FCSTD DOCUMENT  (FreeCAD 0.21RUnknown)
Label: m12_battery_holder
License: All rights reserved
LicenseURL: http://en.wikipedia.org/wiki/All_rights_reserved
objects: Sketcher::SketchObject×1, PartDesign::Body×1, Spreadsheet::Sheet×1
note: 2 computed .brp shape members not serialized (recipe doc carries the construction recipe); baked Part::Feature solids carry a one-line shape summary decoded from their .brp

FEATURE [Sketcher::SketchObject] Sketch002
  FullyConstrained = true
  MapMode = 5
  Support = -> [XY_Plane]
  expr: Constraints[22] = Spreadsheet.Diameter
  expr: Constraints[2] = Spreadsheet.Diameter
  expr: Constraints[9] = Spreadsheet.flat_length
  sketch-geometry (7):
    g0: ArcOfCircle CenterX=-9.5 CenterY=0 CenterZ=0 NormalX=0 NormalY=0 NormalZ=1 AngleXU=0 Radius=9.5 StartAngle=2.12452 EndAngle=5.20586
    g1: ArcOfCircle CenterX=9.5 CenterY=0 CenterZ=0 NormalX=0 NormalY=0 NormalZ=1 AngleXU=0 Radius=9.5 StartAngle=4.21892 EndAngle=7.30025
    g2: ArcOfCircle CenterX=0 CenterY=16.4545 CenterZ=0 NormalX=0 NormalY=0 NormalZ=1 AngleXU=0 Radius=9.5 StartAngle=0.0301294 EndAngle=3.11146
    g3: LineSegment StartX=-5 StartY=-8.3666 StartZ=0 EndX=5 EndY=-8.3666 EndZ=0
    g4: LineSegment StartX=-14.4957 StartY=8.08041 StartZ=0 EndX=-9.49569 EndY=16.7407 EndZ=0
    g5: LineSegment StartX=9.49569 StartY=16.7407 StartZ=0 EndX=14.4957 EndY=8.08041 EndZ=0
    g6: LineSegment StartX=0 StartY=16.4545 StartZ=0 EndX=-9.5 EndY=0 EndZ=0
  constraints (23):
    c: PointOnObject(g0,g-1)
    c: PointOnObject(g-1,g0)
    c: Diameter(g0) = 19
    c: PointOnObject(g1,g-1)
    c: PointOnObject(g-1,g1)
    c: Equal(g0,g1)
    c: PointOnObject(g2,g-2)
    c: Equal(g0,g2)
    c: Horizontal(g3)
    c: DistanceX(g3,g3) = 10
    c: Equal(g4,g5)
    c: Horizontal(g4,g5)
    c: Coincident(g6,g2)
    c: Coincident(g6,g0)
    c: Parallel(g4,g6)
    c: Coincident(g2,g4)
    c: Coincident(g0,g4)
    c: Coincident(g0,g3)
    c: Coincident(g1,g3)
    c: Coincident(g1,g5)
    c: Coincident(g2,g5)
    c: Equal(g4,g3)
    c: Distance(g6) = 19
FEATURE [PartDesign::Body] Body
  Group = -> [Sketch002]
  Origin = -> Origin
FEATURE [Spreadsheet::Sheet] Spreadsheet
  cells = A1='Diameter; B1(Diameter)=19; C1(scaled_diameter)==B1 + B4 * 2; A2='flat length; B2(flat_length)=10; C2(scaled_flat_length)==B2 + B4; A4='thickness; B4=1.5
